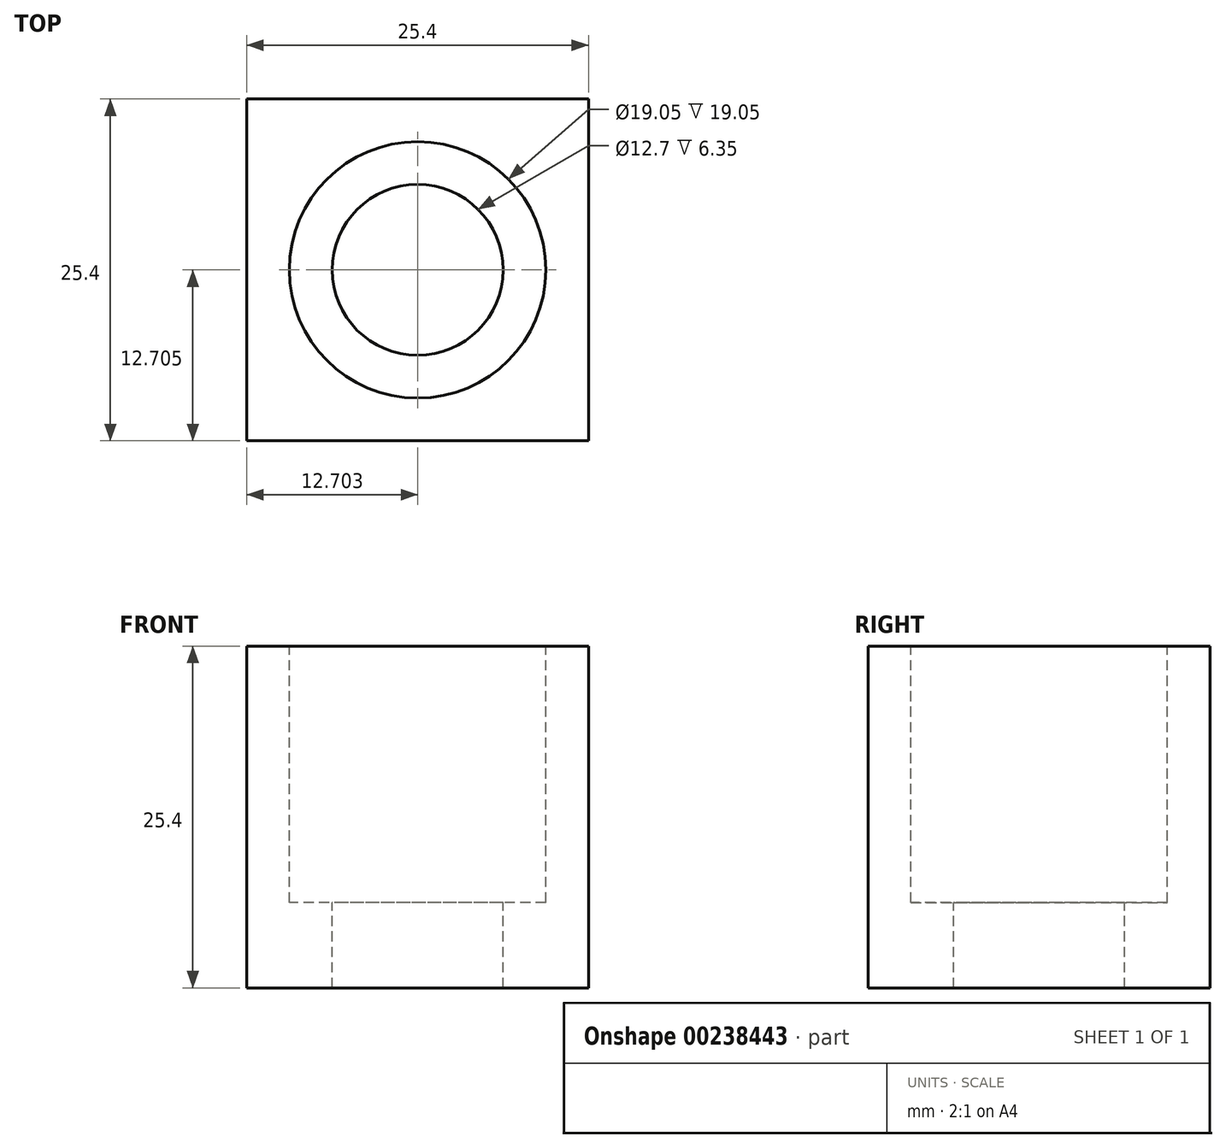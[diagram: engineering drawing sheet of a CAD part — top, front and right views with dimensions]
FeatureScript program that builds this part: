
annotation { "Feature Type Name" : "Feature", "Feature Type Description" : "" }
export const myFeature = defineFeature(function(context is Context, id is Id, definition is map)
    precondition{}
    {
        {
            var Q0;
            Q0=qCreatedBy(makeId("Top.planeOp"),FACE);
            var sketch = newSketch(context, id + "F0", { "sketchPlane" : qUnion([Q0])});
            skLineSegment(sketch, "E0.bottom", {"start": v(-16.28, -5.44) * mm, "end": v(9.12, -5.44) * mm});
            skLineSegment(sketch, "E0.top", {"start": v(-16.28, -30.84) * mm, "end": v(9.12, -30.84) * mm});
            skLineSegment(sketch, "E0.left", {"start": v(-16.28, -5.44) * mm, "end": v(-16.28, -30.84) * mm});
            skLineSegment(sketch, "E0.right", {"start": v(9.12, -5.44) * mm, "end": v(9.12, -30.84) * mm});
            skSolve(sketch);
        }
        {
            var Q0;
            Q0=makeQuery(id+"F0.imprint","IMPRINT",FACE,{"disambiguationData":[TD([[makeQuery(id+"F0.imprint","IMPRINT",EDGE,{"derivedFrom":sQuery(id+"F0.wireOp",EDGE,"E0.bottom")}),-1.0]])]});
            extrude(context, id + "F1", {"entities" : qUnion([Q0]), "depth" : 25.4 * mm});
        }
        {
            var Q0;
            Q0=makeQuery(id+"F1.opExtrude","CAP_FACE",FACE,{"disambiguationData":[OSD([sQuery(id+"F0.wireOp",EDGE,"E0.bottom"),sQuery(id+"F0.wireOp",EDGE,"E0.top"),sQuery(id+"F0.wireOp",EDGE,"E0.left"),sQuery(id+"F0.wireOp",EDGE,"E0.right")])],"isStart":false});
            var sketch = newSketch(context, id + "F2", { "sketchPlane" : qUnion([Q0])});
            skCircle(sketch, "E1", {"center": v(-3.58, -18.14) * mm, "radius": 9.53 * mm});
            skPoint(sketch, "E1.centerSnap0", {"position": v(-16.28, -18.14) * mm});
            skPoint(sketch, "E1.centerSnap1", {"position": v(-3.58, -30.84) * mm});
            skSolve(sketch);
        }
        {
            var Q0;
            Q0 = qSketchRegion(id + "F2", true);
            var Q1;
            Q1=sQuery(id+"F2.wireOp",EDGE,"E1");
            extrude(context, id + "F3", {"entities" : qUnion([Q0]), "operationType" : NewBodyOperationType.REMOVE, "surfaceEntities" : qUnion([Q1]), "oppositeDirection" : true, "depth" : 19.05 * mm});
        }
        {
            var Q0;
            Q0=makeQuery(id+"F3.boolean.opBoolean","COPY",FACE,{"derivedFrom":makeQuery(id+"F3.opExtrude","CAP_FACE",FACE,{"disambiguationData":[OSD([sQuery(id+"F2.wireOp",EDGE,"E1")])],"isStart":false})});
            var sketch = newSketch(context, id + "F4", { "sketchPlane" : qUnion([Q0])});
            skCircle(sketch, "E2", {"center": v(-3.58, -18.14) * mm, "radius": 6.35 * mm});
            skSolve(sketch);
        }
        {
            var Q0;
            Q0 = qSketchRegion(id + "F4", true);
            var Q1;
            Q1=makeQuery(id+"F4.imprint","IMPRINT",FACE,{"disambiguationData":[TD([[makeQuery(id+"F4.imprint","IMPRINT",EDGE,{"derivedFrom":sQuery(id+"F4.wireOp",EDGE,"E2")}),1.0]])]});
            extrude(context, id + "F5", {"entities" : qUnion([Q0, Q1]), "operationType" : NewBodyOperationType.REMOVE, "endBound" : BoundingType.THROUGH_ALL, "oppositeDirection" : true, "depth" : 25.4 * mm});
        }
    });
